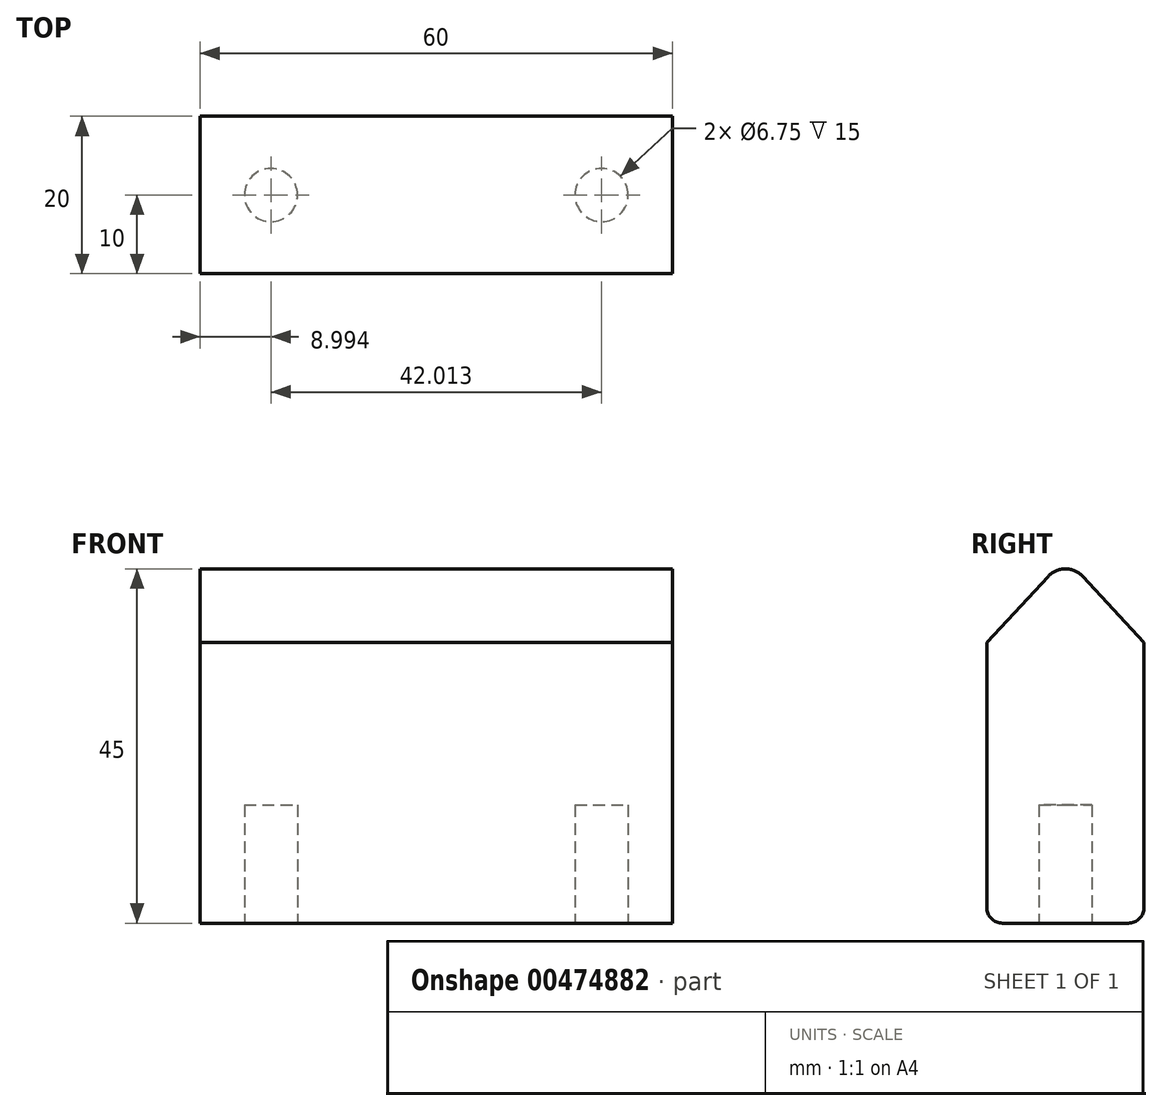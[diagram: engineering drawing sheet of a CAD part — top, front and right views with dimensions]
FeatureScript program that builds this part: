
annotation { "Feature Type Name" : "Feature", "Feature Type Description" : "" }
export const myFeature = defineFeature(function(context is Context, id is Id, definition is map)
    precondition{}
    {
        {
            var Q0;
            Q0=qCreatedBy(makeId("Right.planeOp"),FACE);
            var sketch = newSketch(context, id + "F0", { "sketchPlane" : qUnion([Q0])});
            skLineSegment(sketch, "E0.top", {"start": v(0, -35.68) * mm, "end": v(20, -35.68) * mm});
            skLineSegment(sketch, "E0.left", {"start": v(0, 0) * mm, "end": v(0, -35.68) * mm});
            skLineSegment(sketch, "E0.right", {"start": v(20, 0) * mm, "end": v(20, -35.68) * mm});
            skLineSegment(sketch, "E1", {"start": v(0, 0) * mm, "end": v(7.8, 8.37) * mm});
            skLineSegment(sketch, "E2", {"start": v(20, 0) * mm, "end": v(12.2, 8.37) * mm});
            skPoint(sketch, "E3.visualSharp", {"position": v(10, 10.72) * mm});
            skArc(sketch, "E3.filletArc", {"start": v(12.2, 8.37) * mm, "mid": v(10, 9.32) * mm, "end": v(7.8, 8.37) * mm});
            skSolve(sketch);
        }
        {
            var Q0;
            Q0=makeQuery(id+"F0.imprint","IMPRINT",FACE,{"disambiguationData":[TD([[makeQuery(id+"F0.imprint","IMPRINT",EDGE,{"derivedFrom":sQuery(id+"F0.wireOp",EDGE,"E0.top")}),1.0]])]});
            extrude(context, id + "F1", {"entities" : qUnion([Q0]), "depth" : 60 * mm});
        }
        {
            var Q0;
            Q0=makeQuery(id+"F1.opExtrude","SWEPT_FACE",FACE,{"disambiguationData":[OSD([sQuery(id+"F0.wireOp",EDGE,"E0.top")])]});
            var sketch = newSketch(context, id + "F2", { "sketchPlane" : qUnion([Q0])});
            skCircle(sketch, "E4", {"center": v(9, -10) * mm, "radius": 3.38 * mm});
            skPoint(sketch, "E4.centerSnap0", {"position": v(0, -10) * mm});
            skCircle(sketch, "E5", {"center": v(51, -10) * mm, "radius": 3.38 * mm});
            skPoint(sketch, "E5.centerSnap0", {"position": v(60, -10) * mm});
            skSolve(sketch);
        }
        {
            var Q0;
            Q0 = qSketchRegion(id + "F2", true);
            extrude(context, id + "F3", {"entities" : qUnion([Q0]), "operationType" : NewBodyOperationType.REMOVE, "oppositeDirection" : true, "depth" : 15 * mm});
        }
        {
            var Q0;
            Q0=makeQuery(id+"F1.opExtrude","SWEPT_EDGE",EDGE,{"disambiguationData":[OSD([sQuery(id+"F0.wireOp",EDGE,"E0.top"),sQuery(id+"F0.wireOp",EDGE,"E0.right")])]});
            var Q1;
            Q1=makeQuery(id+"F1.opExtrude","SWEPT_EDGE",EDGE,{"disambiguationData":[OSD([sQuery(id+"F0.wireOp",EDGE,"E0.top"),sQuery(id+"F0.wireOp",EDGE,"E0.left")])]});
            fillet(context, id + "F4", {"entities" : qUnion([Q0, Q1]), "radius" : 2 * mm, "tangentPropagation" : true, "allowEdgeOverflow" : false});
        }
    });
